# Revit family: Door_Overhead-Coiling_WalzKrenzer_AutoSeal
name_source: partatom
category: Doors
units: mm (PartAtom-declared; Revit-internal decimal feet)

## family parameters
Always vertical = Yes
Classification Number = 23.30.10.21.37.17
Cut with Voids When Loaded = No
Host = Wall
Room Calculation Point = No
Shared = No

## types (1)
- as Specified
    Assembly Code = E1090900
    Description = Walz and Krenzer Automatic AutoSeal Watertight Roller Curtain Door - as Specified
    Expected Lifespan (Years) = 0
    Fire Rating = as Specified
    Function = Interior
    Has Battery Backup = Yes
    Jamb Thickness_Sides = 0' - 4 5/16"
    Keynote = 08392
    Maintenance Schedule (Months) = 0
    Manufacturer = Walz & Krenzer, Inc.
    Manufacturer Fax = 203-267-5716
    Manufacturer Website = http://www.floodbarriers.com
    Model = WT-R
    Panel Thickness = 0' - 1"
    Product Data = http://www.arcat.com
    RO Spacing Sides = 0' - 0 1/2"
    RO Spacing Top = 0' - 0 1/2"
    Sales Information = http://www.floodbarriers.com
    Specification = http://www.arcat.com
    URL = http://www.floodbarriers.com
    Wall Closure = By host
    Warranty Duration (Years) = 0

## geometry (parser evidence)
native form markers: Sweep x2
no freeform markers — native parametric forms only
